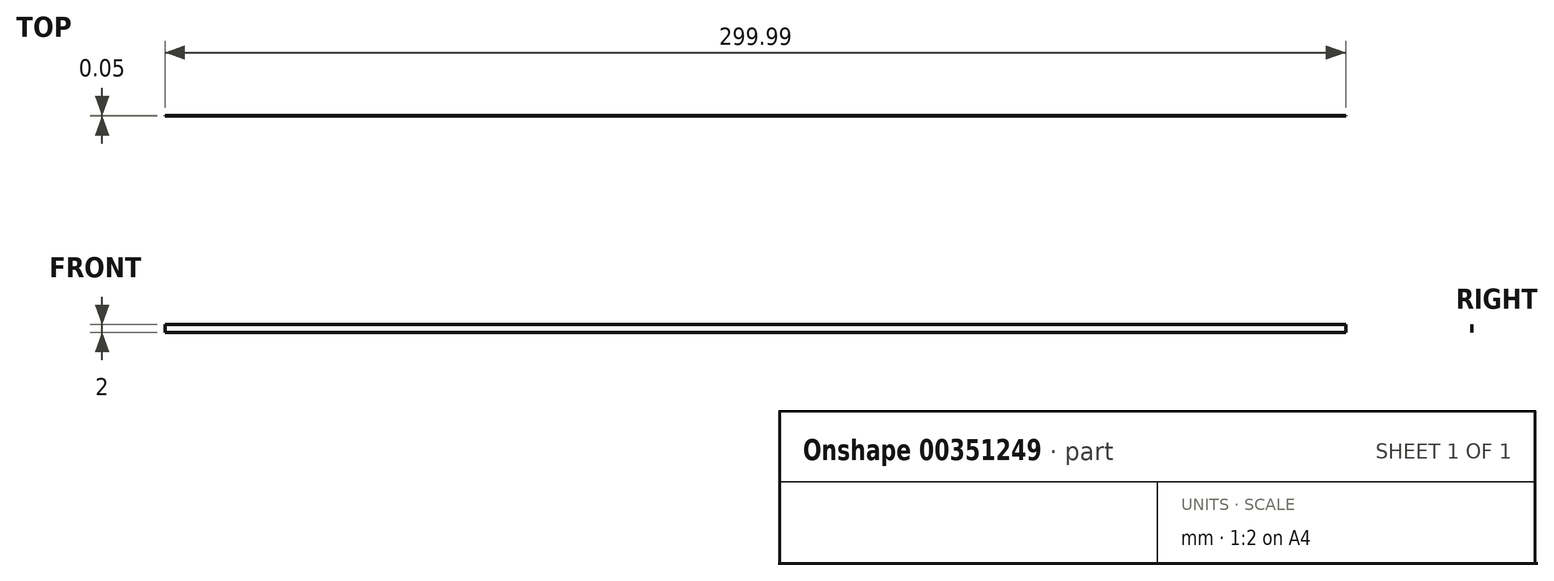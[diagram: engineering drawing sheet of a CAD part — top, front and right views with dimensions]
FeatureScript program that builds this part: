
annotation { "Feature Type Name" : "Feature", "Feature Type Description" : "" }
export const myFeature = defineFeature(function(context is Context, id is Id, definition is map)
    precondition{}
    {
        {
            var Q0;
            Q0=qCreatedBy(makeId("Front.planeOp"),FACE);
            var sketch = newSketch(context, id + "F0", { "sketchPlane" : qUnion([Q0])});
            skLineSegment(sketch, "E0.bottom", {"start": v(-100.68, 0) * mm, "end": v(199.31, 0) * mm});
            skLineSegment(sketch, "E0.top", {"start": v(-100.68, -2) * mm, "end": v(199.31, -2) * mm});
            skLineSegment(sketch, "E0.left", {"start": v(-100.68, 0) * mm, "end": v(-100.68, -2) * mm});
            skLineSegment(sketch, "E0.right", {"start": v(199.31, 0) * mm, "end": v(199.31, -2) * mm});
            skSolve(sketch);
        }
        {
            var Q0;
            Q0 = qSketchRegion(id + "F0", true);
            extrude(context, id + "F1", {"entities" : qUnion([Q0]), "oppositeDirection" : true, "depth" : 0.05 * mm});
        }
    });
